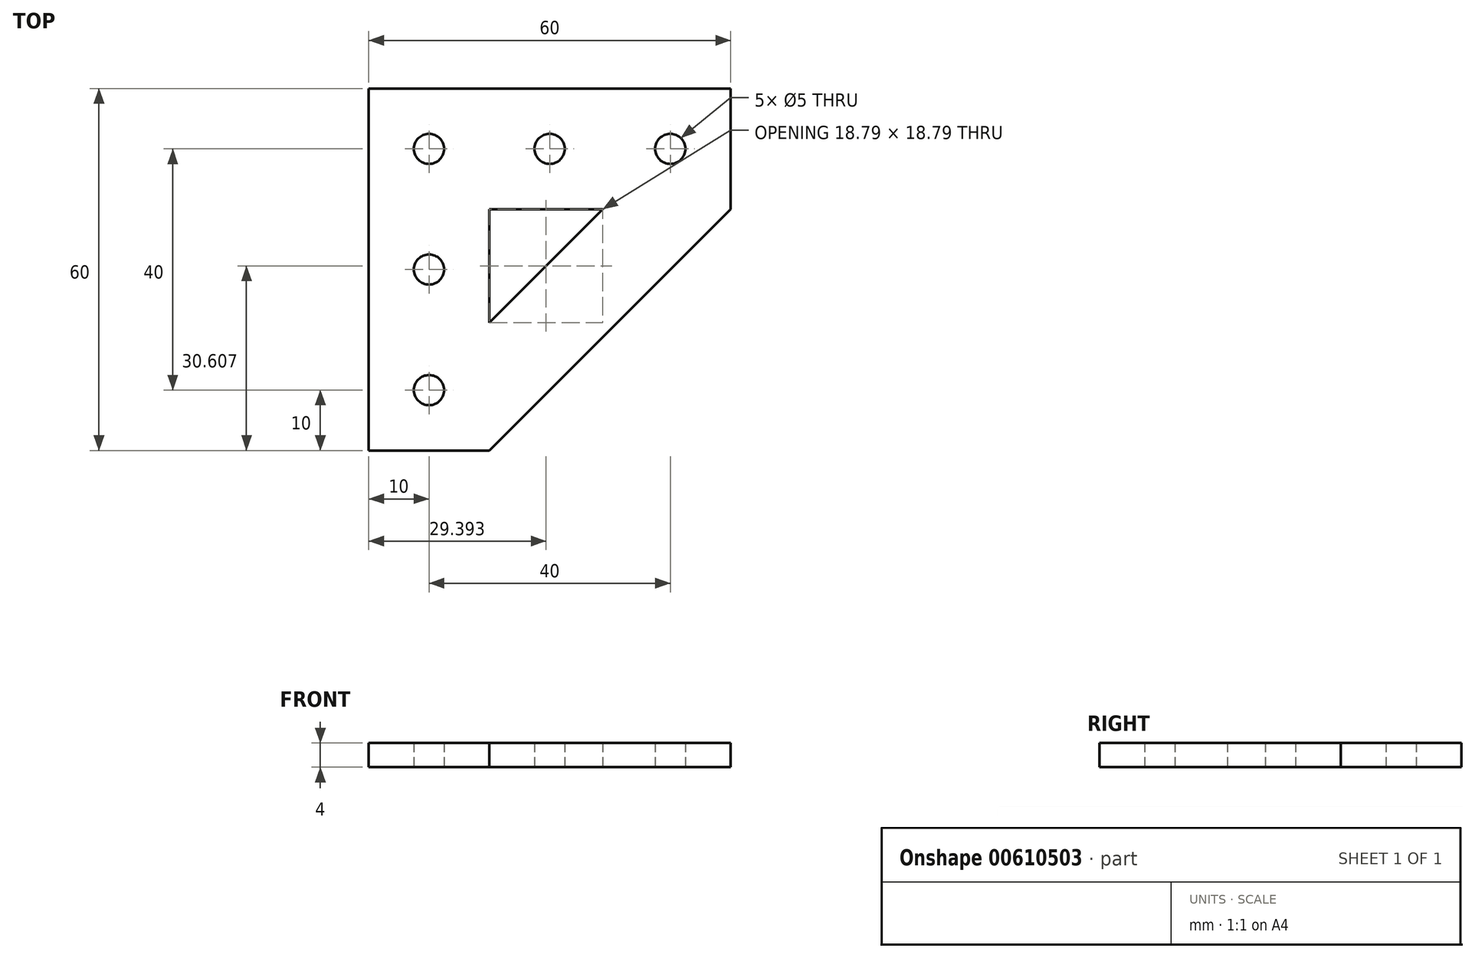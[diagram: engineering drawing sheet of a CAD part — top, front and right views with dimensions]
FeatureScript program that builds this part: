
annotation { "Feature Type Name" : "Feature", "Feature Type Description" : "" }
export const myFeature = defineFeature(function(context is Context, id is Id, definition is map)
    precondition{}
    {
        {
            var Q0;
            Q0=qCreatedBy(makeId("Top.planeOp"),FACE);
            var sketch = newSketch(context, id + "F0", { "sketchPlane" : qUnion([Q0])});
            skLineSegment(sketch, "E0.bottom", {"start": v(-30, 30) * mm, "end": v(30, 30) * mm});
            skLineSegment(sketch, "E0.top", {"start": v(-30, -30) * mm, "end": v(30, -30) * mm});
            skLineSegment(sketch, "E0.left", {"start": v(-30, 30) * mm, "end": v(-30, -30) * mm});
            skLineSegment(sketch, "E0.right", {"start": v(30, 30) * mm, "end": v(30, -30) * mm});
            skPoint(sketch, "E0.middle", {"position": v(0, 0) * mm});
            skPoint(sketch, "E1", {"position": v(-10, -30) * mm});
            skPoint(sketch, "E2", {"position": v(30, 10) * mm});
            skLineSegment(sketch, "E3", {"start": v(30, 10) * mm, "end": v(-10, -30) * mm});
            skLineSegment(sketch, "E4", {"start": v(-10, -30) * mm, "end": v(-10, 10) * mm, "construction": true});
            skLineSegment(sketch, "E5", {"start": v(-10, 10) * mm, "end": v(30, 10) * mm, "construction": true});
            skLineSegment(sketch, "E6", {"start": v(-10, -8.79) * mm, "end": v(8.79, 10) * mm});
            skPoint(sketch, "E6.endSnap0", {"position": v(10, 10) * mm});
            skPoint(sketch, "E7", {"position": v(-20, -30) * mm});
            skPoint(sketch, "E8", {"position": v(-30, 20) * mm});
            skPoint(sketch, "E9", {"position": v(-20, 20) * mm});
            skPoint(sketch, "E10", {"position": v(0, 20) * mm});
            skPoint(sketch, "E11", {"position": v(20, 20) * mm});
            skPoint(sketch, "E12", {"position": v(-20, -20) * mm});
            skPoint(sketch, "E13", {"position": v(-20, 0) * mm});
            skCircle(sketch, "E14", {"center": v(-20, 20) * mm, "radius": 2.5 * mm});
            skCircle(sketch, "E15", {"center": v(0, 20) * mm, "radius": 2.5 * mm});
            skCircle(sketch, "E16", {"center": v(20, 20) * mm, "radius": 2.5 * mm});
            skCircle(sketch, "E17", {"center": v(-20, 0) * mm, "radius": 2.5 * mm});
            skCircle(sketch, "E18", {"center": v(-20, -20) * mm, "radius": 2.5 * mm});
            skLineSegment(sketch, "E19", {"start": v(-10, -8.79) * mm, "end": v(-10, 10) * mm});
            skLineSegment(sketch, "E20", {"start": v(-10, 10) * mm, "end": v(8.79, 10) * mm});
            skSolve(sketch);
        }
        {
            var Q0;
            Q0=makeQuery(id+"F0.imprint","IMPRINT",FACE,{"disambiguationData":[TD([[makeQuery(id+"F0.imprint","IMPRINT",EDGE,{"derivedFrom":sQuery(id+"F0.wireOp",EDGE,"E0.bottom")}),-1.0]])]});
            extrude(context, id + "F1", {"entities" : qUnion([Q0]), "depth" : 4 * mm, "offsetDistance" : 25 * mm});
        }
    });
